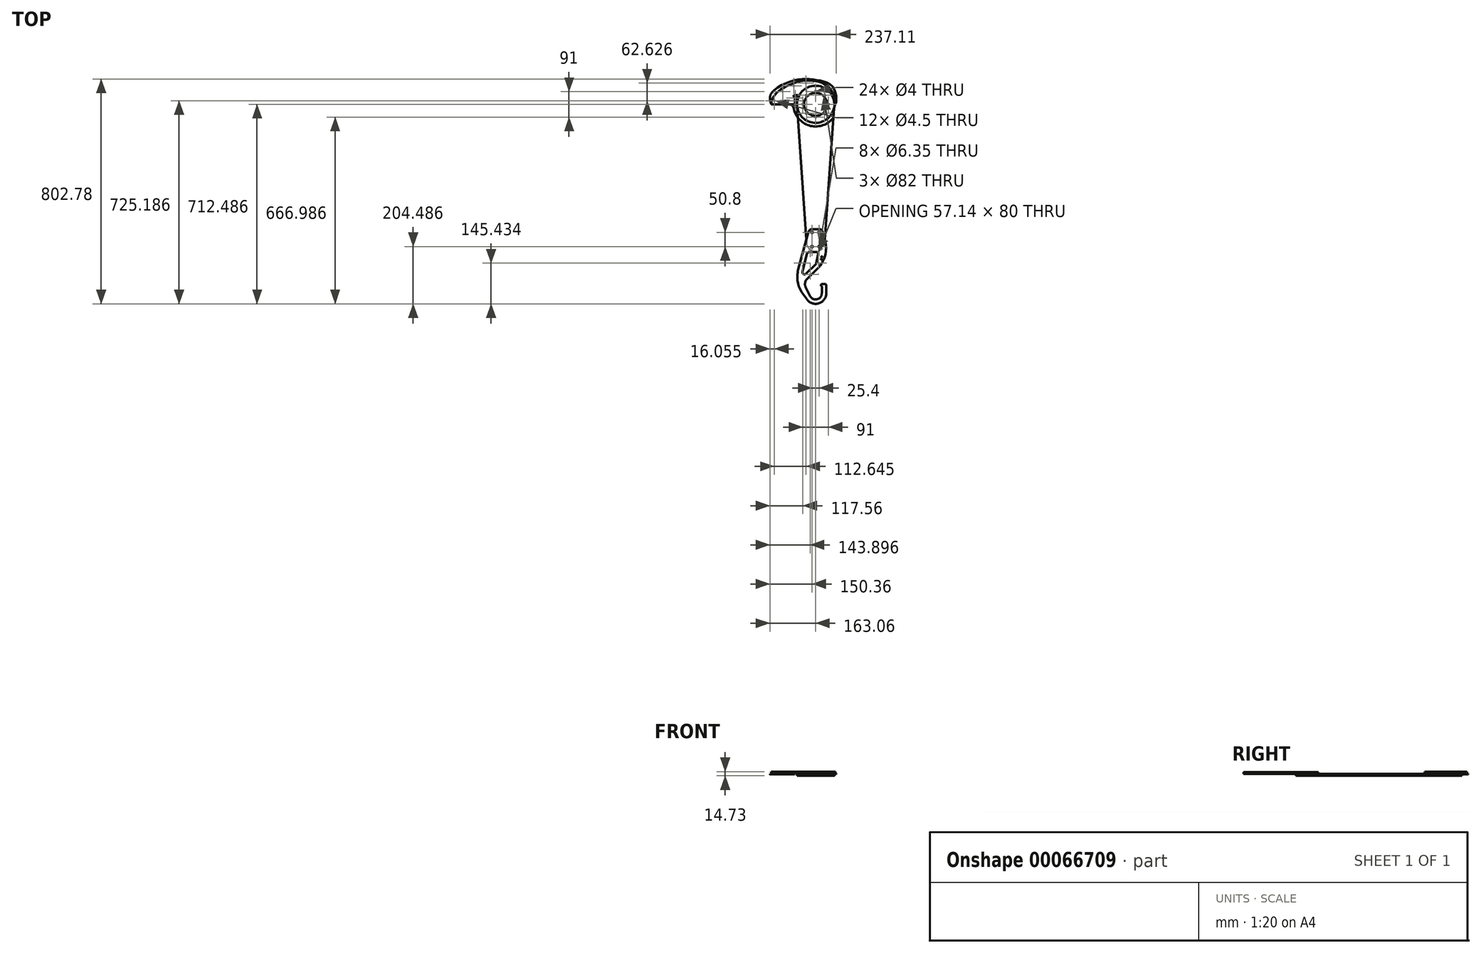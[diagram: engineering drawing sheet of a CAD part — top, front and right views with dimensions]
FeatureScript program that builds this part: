
annotation { "Feature Type Name" : "Feature", "Feature Type Description" : "" }
export const myFeature = defineFeature(function(context is Context, id is Id, definition is map)
    precondition{}
    {
        {
            var Q0;
            Q0=qCreatedBy(makeId("Top.planeOp"),FACE);
            var sketch = newSketch(context, id + "F0", { "sketchPlane" : qUnion([Q0])});
            skLineSegment(sketch, "E0", {"start": v(-316.24, 303.68) * mm, "end": v(-281.67, -188.68) * mm});
            skLineSegment(sketch, "E1", {"start": v(-218.33, -188.68) * mm, "end": v(-183.76, 303.68) * mm});
            skArc(sketch, "E2", {"start": v(-183.76, 303.68) * mm, "mid": v(-250, 374.73) * mm, "end": v(-316.24, 303.68) * mm});
            skArc(sketch, "E3", {"start": v(-281.67, -188.68) * mm, "mid": v(-250, -218.2) * mm, "end": v(-218.33, -188.68) * mm});
            skLineSegment(sketch, "E4.bottom", {"start": v(-237.3, -148.87) * mm, "end": v(-262.7, -148.87) * mm, "construction": true});
            skLineSegment(sketch, "E4.top", {"start": v(-237.3, -199.67) * mm, "end": v(-262.7, -199.67) * mm, "construction": true});
            skLineSegment(sketch, "E4.left", {"start": v(-237.3, -148.87) * mm, "end": v(-237.3, -199.67) * mm, "construction": true});
            skLineSegment(sketch, "E4.right", {"start": v(-262.7, -148.87) * mm, "end": v(-262.7, -199.67) * mm, "construction": true});
            skCircle(sketch, "E5", {"center": v(-237.3, -199.67) * mm, "radius": 3.18 * mm});
            skCircle(sketch, "E6", {"center": v(-237.3, -148.87) * mm, "radius": 3.18 * mm});
            skCircle(sketch, "E7", {"center": v(-262.7, -199.67) * mm, "radius": 3.18 * mm});
            skCircle(sketch, "E8", {"center": v(-262.7, -148.87) * mm, "radius": 3.18 * mm});
            skLineSegment(sketch, "E9", {"start": v(-250, -186.97) * mm, "end": v(-250, -317.53) * mm, "construction": true});
            skLineSegment(sketch, "E10", {"start": v(-204.75, -174.27) * mm, "end": v(-310.47, -174.27) * mm, "construction": true});
            skSolve(sketch);
        }
        {
            var Q0;
            Q0 = qSketchRegion(id + "F0", true);
            extrude(context, id + "F1", {"entities" : qUnion([Q0]), "depth" : 7.37 * mm});
        }
        {
            var Q0;
            Q0=makeQuery(id+"F1.opExtrude","CAP_FACE",FACE,{"disambiguationData":[OSD([sQuery(id+"F0.wireOp",EDGE,"E0"),sQuery(id+"F0.wireOp",EDGE,"E1"),sQuery(id+"F0.wireOp",EDGE,"E2"),sQuery(id+"F0.wireOp",EDGE,"E3")])],"isStart":false});
            var sketch = newSketch(context, id + "F2", { "sketchPlane" : qUnion([Q0])});
            skCircle(sketch, "E11", {"center": v(-250, 308.33) * mm, "radius": 41 * mm});
            skSolve(sketch);
        }
        {
            var Q0;
            Q0=makeQuery(id+"F2.imprint","IMPRINT",FACE,{"disambiguationData":[TD([[makeQuery(id+"F2.imprint","IMPRINT",EDGE,{"derivedFrom":sQuery(id+"F2.wireOp",EDGE,"E11")}),1.0]])]});
            extrude(context, id + "F3", {"entities" : qUnion([Q0]), "operationType" : NewBodyOperationType.REMOVE, "oppositeDirection" : true, "depth" : 25.4 * mm});
        }
        {
            var Q0;
            Q0=makeQuery(id+"F1.opExtrude","CAP_FACE",FACE,{"disambiguationData":[OSD([sQuery(id+"F0.wireOp",EDGE,"E0"),sQuery(id+"F0.wireOp",EDGE,"E1"),sQuery(id+"F0.wireOp",EDGE,"E2"),sQuery(id+"F0.wireOp",EDGE,"E3"),sQuery(id+"F0.wireOp",EDGE,"E5"),sQuery(id+"F0.wireOp",EDGE,"E6"),sQuery(id+"F0.wireOp",EDGE,"E7"),sQuery(id+"F0.wireOp",EDGE,"E8")])],"isStart":false});
            var sketch = newSketch(context, id + "F4", { "sketchPlane" : qUnion([Q0])});
            skLineSegment(sketch, "E12", {"start": v(-250, -72.28) * mm, "end": v(-250, -435.83) * mm, "construction": true});
            skCircle(sketch, "E13", {"center": v(-250, -366.06) * mm, "radius": 19.05 * mm, "construction": true});
            skCircle(sketch, "E14.0", {"center": v(-262.7, -148.87) * mm, "radius": 3.18 * mm});
            skCircle(sketch, "E14.1", {"center": v(-237.3, -148.87) * mm, "radius": 3.18 * mm});
            skCircle(sketch, "E14.2", {"center": v(-237.3, -199.67) * mm, "radius": 3.18 * mm});
            skCircle(sketch, "E14.3", {"center": v(-262.7, -199.67) * mm, "radius": 3.18 * mm});
            skCircle(sketch, "E15", {"center": v(-250, -366.06) * mm, "radius": 22.23 * mm});
            skLineSegment(sketch, "E16", {"start": v(-200.62, -235.34) * mm, "end": v(-293.23, -327.96) * mm});
            skLineSegment(sketch, "E17", {"start": v(-211.9, -241.78) * mm, "end": v(-211.9, -137.46) * mm, "construction": true});
            skLineSegment(sketch, "E18", {"start": v(-227.24, -137.46) * mm, "end": v(-272.76, -137.46) * mm});
            skLineSegment(sketch, "E19", {"start": v(-324.58, -327.96) * mm, "end": v(-280.87, -388.39) * mm});
            skArc(sketch, "E20", {"start": v(-280.87, -388.39) * mm, "mid": v(-238.26, -402.3) * mm, "end": v(-211.9, -366.06) * mm});
            skLineSegment(sketch, "E21", {"start": v(-211.9, -366.06) * mm, "end": v(-211.9, -333.02) * mm});
            skLineSegment(sketch, "E22", {"start": v(-211.9, -333.02) * mm, "end": v(-230.95, -333.02) * mm});
            skLineSegment(sketch, "E23", {"start": v(-230.95, -333.02) * mm, "end": v(-230.95, -339.37) * mm});
            skLineSegment(sketch, "E24", {"start": v(-230.95, -339.37) * mm, "end": v(-227.78, -339.37) * mm});
            skLineSegment(sketch, "E25", {"start": v(-227.78, -366.06) * mm, "end": v(-227.78, -339.37) * mm});
            skCircle(sketch, "E26", {"center": v(-229.53, -244.44) * mm, "radius": 1.75 * mm});
            skCircle(sketch, "E27", {"center": v(-227.78, -236.5) * mm, "radius": 1.75 * mm});
            skArc(sketch, "E28", {"start": v(-227.78, -345.72) * mm, "mid": v(-277.64, -333.68) * mm, "end": v(-316.5, -300.2) * mm, "construction": true});
            skCircle(sketch, "E29", {"center": v(-247.79, -316.19) * mm, "radius": 23.81 * mm, "construction": true});
            skLineSegment(sketch, "E30", {"start": v(-230.95, -333.02) * mm, "end": v(-264.63, -299.35) * mm, "construction": true});
            skLineSegment(sketch, "E31", {"start": v(-293.23, -327.96) * mm, "end": v(-269.99, -375.77) * mm});
            skPoint(sketch, "E32", {"position": v(-250, 308.33) * mm});
            skLineSegment(sketch, "E33", {"start": v(-272.76, -137.46) * mm, "end": v(-324.58, -327.96) * mm});
            skLineSegment(sketch, "E34", {"start": v(-227.24, -137.46) * mm, "end": v(-200.62, -235.34) * mm});
            skLineSegment(sketch, "E35", {"start": v(-284.2, -296.47) * mm, "end": v(-249.4, -261.67) * mm});
            skLineSegment(sketch, "E36", {"start": v(-272.35, -218.72) * mm, "end": v(-248.53, -218.72) * mm});
            skLineSegment(sketch, "E37.trimOffspring", {"start": v(-280, -224.58) * mm, "end": v(-297.47, -288.77) * mm});
            skLineSegment(sketch, "E38", {"start": v(-247.26, -257.77) * mm, "end": v(-240.78, -228.37) * mm});
            skPoint(sketch, "E39.visualSharp", {"position": v(-305.3, -317.58) * mm});
            skArc(sketch, "E39.filletArc", {"start": v(-297.47, -288.77) * mm, "mid": v(-293.8, -297.72) * mm, "end": v(-284.2, -296.47) * mm});
            skPoint(sketch, "E40.visualSharp", {"position": v(-278.41, -218.72) * mm});
            skArc(sketch, "E40.filletArc", {"start": v(-272.35, -218.72) * mm, "mid": v(-277.17, -220.36) * mm, "end": v(-280, -224.58) * mm});
            skPoint(sketch, "E41.visualSharp", {"position": v(-238.65, -218.72) * mm});
            skArc(sketch, "E41.filletArc", {"start": v(-240.78, -228.37) * mm, "mid": v(-242.34, -221.69) * mm, "end": v(-248.53, -218.72) * mm});
            skPoint(sketch, "E42.visualSharp", {"position": v(-247.76, -260.03) * mm});
            skArc(sketch, "E42.filletArc", {"start": v(-249.4, -261.67) * mm, "mid": v(-248.05, -259.87) * mm, "end": v(-247.26, -257.77) * mm});
            skSolve(sketch);
        }
        {
            var Q0;
            {var subQ8=sQuery(id+"F4.wireOp",EDGE,"E20");Q0=makeQuery(id+"F4.imprint","IMPRINT",FACE,{"disambiguationData":[TD([[makeQuery(id+"F4.imprint","IMPRINT",EDGE,{"derivedFrom":subQ8}),1.0]])]});}
            var Q1;
            Q1=makeQuery(id+"F4.imprint","IMPRINT",FACE,{"disambiguationData":[TD([[makeQuery(id+"F4.imprint","IMPRINT",EDGE,{"derivedFrom":sQuery(id+"F4.wireOp",EDGE,"E14.0")}),-1.0]])]});
            extrude(context, id + "F5", {"entities" : qUnion([Q0, Q1]), "depth" : 6.35 * mm});
        }
        {
            var Q0;
            Q0=makeQuery(id+"F5.opExtrude","SWEPT_EDGE",EDGE,{"disambiguationData":[OSD([sQuery(id+"F4.wireOp",EDGE,"E18"),sQuery(id+"F4.wireOp",EDGE,"E33")])]});
            var Q1;
            Q1=makeQuery(id+"F5.opExtrude","SWEPT_EDGE",EDGE,{"disambiguationData":[OSD([sQuery(id+"F4.wireOp",EDGE,"E18"),sQuery(id+"F4.wireOp",EDGE,"E34")])]});
            fillet(context, id + "F6", {"entities" : qUnion([Q0, Q1]), "radius" : 12.7 * mm, "tangentPropagation" : true, "allowEdgeOverflow" : false});
        }
        {
            var Q0;
            Q0=makeQuery(id+"F5.opExtrude","SWEPT_EDGE",EDGE,{"disambiguationData":[OSD([sQuery(id+"F4.wireOp",EDGE,"E16"),sQuery(id+"F4.wireOp",EDGE,"E31")])]});
            fillet(context, id + "F7", {"entities" : qUnion([Q0]), "radius" : 25.4 * mm, "tangentPropagation" : true, "allowEdgeOverflow" : false});
        }
        {
            var Q0;
            Q0=makeQuery(id+"F5.opExtrude","SWEPT_EDGE",EDGE,{"disambiguationData":[OSD([sQuery(id+"F4.wireOp",EDGE,"E16"),sQuery(id+"F4.wireOp",EDGE,"E17")])]});
            var Q1;
            Q1=makeQuery(id+"F5.opExtrude","SWEPT_EDGE",EDGE,{"disambiguationData":[OSD([sQuery(id+"F4.wireOp",EDGE,"E19"),sQuery(id+"F4.wireOp",EDGE,"E33")])]});
            fillet(context, id + "F8", {"entities" : qUnion([Q0, Q1]), "radius" : 101.6 * mm, "tangentPropagation" : true, "allowEdgeOverflow" : false});
        }
        {
            var Q0;
            Q0=makeQuery(id+"F5.opExtrude","SWEPT_EDGE",EDGE,{"disambiguationData":[OSD([sQuery(id+"F4.wireOp",EDGE,"E22"),sQuery(id+"F4.wireOp",EDGE,"E23")])]});
            var Q1;
            Q1=makeQuery(id+"F5.opExtrude","SWEPT_EDGE",EDGE,{"disambiguationData":[OSD([sQuery(id+"F4.wireOp",EDGE,"E21"),sQuery(id+"F4.wireOp",EDGE,"E22")])]});
            fillet(context, id + "F9", {"entities" : qUnion([Q0, Q1]), "radius" : 4.76 * mm, "tangentPropagation" : true, "allowEdgeOverflow" : false});
        }
        {
            var Q0;
            Q0=makeQuery(id+"F5.opExtrude","SWEPT_EDGE",EDGE,{"disambiguationData":[OSD([sQuery(id+"F4.wireOp",EDGE,"E24"),sQuery(id+"F4.wireOp",EDGE,"E25")])]});
            fillet(context, id + "F10", {"entities" : qUnion([Q0]), "radius" : 3.97 * mm, "tangentPropagation" : true, "allowEdgeOverflow" : false});
        }
        {
            var Q0;
            {var subQ0=makeQuery(id+"F1.opExtrude","CAP_EDGE",EDGE,{"disambiguationData":[OSD([sQuery(id+"F0.wireOp",EDGE,"E2")])],"isStart":false});Q0=makeQuery(id+"F4.imprint","IMPRINT",FACE,{"disambiguationData":[TD([[makeQuery(id+"F4.imprint","IMPRINT",EDGE,{"derivedFrom":subQ0}),1.0]])]});}
            var sketch = newSketch(context, id + "F11", { "sketchPlane" : qUnion([Q0])});
            skCircle(sketch, "E43.cCircle", {"center": v(-250, 308.33) * mm, "radius": 45.5 * mm, "construction": true});
            skLineSegment(sketch, "E43.0", {"start": v(-217.83, 276.15) * mm, "end": v(-250, 262.83) * mm, "construction": true});
            skLineSegment(sketch, "E43.1", {"start": v(-250, 262.83) * mm, "end": v(-282.17, 276.15) * mm, "construction": true});
            skLineSegment(sketch, "E43.2", {"start": v(-282.17, 276.15) * mm, "end": v(-295.5, 308.33) * mm, "construction": true});
            skLineSegment(sketch, "E43.3", {"start": v(-295.5, 308.33) * mm, "end": v(-282.17, 340.5) * mm, "construction": true});
            skLineSegment(sketch, "E43.4", {"start": v(-282.17, 340.5) * mm, "end": v(-250, 353.83) * mm, "construction": true});
            skLineSegment(sketch, "E43.5", {"start": v(-250, 353.83) * mm, "end": v(-217.83, 340.5) * mm, "construction": true});
            skLineSegment(sketch, "E43.6", {"start": v(-217.83, 340.5) * mm, "end": v(-204.5, 308.33) * mm, "construction": true});
            skLineSegment(sketch, "E43.7", {"start": v(-204.5, 308.33) * mm, "end": v(-217.83, 276.15) * mm, "construction": true});
            skCircle(sketch, "E44", {"center": v(-217.83, 276.15) * mm, "radius": 2 * mm});
            skCircle(sketch, "E45", {"center": v(-250, 262.83) * mm, "radius": 2 * mm});
            skCircle(sketch, "E46", {"center": v(-282.17, 276.15) * mm, "radius": 2 * mm});
            skCircle(sketch, "E47", {"center": v(-295.5, 308.33) * mm, "radius": 2 * mm});
            skCircle(sketch, "E48", {"center": v(-282.17, 340.5) * mm, "radius": 2 * mm});
            skCircle(sketch, "E49", {"center": v(-250, 353.83) * mm, "radius": 2 * mm});
            skCircle(sketch, "E50", {"center": v(-217.83, 340.5) * mm, "radius": 2 * mm});
            skCircle(sketch, "E51", {"center": v(-204.5, 308.33) * mm, "radius": 2 * mm});
            skSolve(sketch);
        }
        {
            var Q0;
            Q0 = qSketchRegion(id + "F11", true);
            extrude(context, id + "F12", {"entities" : qUnion([Q0]), "operationType" : NewBodyOperationType.REMOVE, "endBound" : BoundingType.THROUGH_ALL, "oppositeDirection" : true, "depth" : 25.4 * mm});
        }
        {
            var Q0;
            Q0=makeQuery(id+"F2.imprint","IMPRINT",FACE,{"disambiguationData":[TD([[makeQuery(id+"F2.imprint","IMPRINT",EDGE,{"derivedFrom":sQuery(id+"F2.wireOp",EDGE,"E11")}),-1.0]])]});
            var sketch = newSketch(context, id + "F13", { "sketchPlane" : qUnion([Q0])});
            skFitSpline(sketch, "E52", {"points": [v(-180.15, 308.33) * mm, v(-196.12, 362.2) * mm, v(-250, 390.88) * mm, v(-326.33, 384.66) * mm, v(-408.75, 308.33) * mm], "startDerivative": vector(54.67, 167.45) * mm, "endDerivative": vector(0, -373.77) * mm});
            skLineSegment(sketch, "E53", {"start": v(-408.75, 308.33) * mm, "end": v(-250, 308.33) * mm});
            skLineSegment(sketch, "E54", {"start": v(-250, 308.33) * mm, "end": v(-326.33, 384.66) * mm, "construction": true});
            skLineSegment(sketch, "E55", {"start": v(-250, 308.33) * mm, "end": v(-250, 390.88) * mm, "construction": true});
            skLineSegment(sketch, "E56", {"start": v(-250, 308.33) * mm, "end": v(-196.12, 362.2) * mm, "construction": true});
            skLineSegment(sketch, "E57", {"start": v(-250, 308.33) * mm, "end": v(-180.15, 308.33) * mm});
            skCircle(sketch, "E58", {"center": v(-250, 308.33) * mm, "radius": 66.4 * mm});
            skLineSegment(sketch, "E59", {"start": v(-186.88, 287.72) * mm, "end": v(-180.15, 308.33) * mm});
            skLineSegment(sketch, "E60", {"start": v(-324.34, 308.33) * mm, "end": v(-324.34, 333.73) * mm});
            skLineSegment(sketch, "E61", {"start": v(-316.4, 308.33) * mm, "end": v(-316.4, 333.73) * mm});
            skArc(sketch, "E62", {"start": v(-324.34, 341.66) * mm, "mid": v(-328.3, 337.7) * mm, "end": v(-324.34, 333.73) * mm});
            skArc(sketch, "E63", {"start": v(-316.4, 333.73) * mm, "mid": v(-312.43, 337.7) * mm, "end": v(-316.4, 341.66) * mm});
            skLineSegment(sketch, "E64", {"start": v(-324.34, 341.66) * mm, "end": v(-316.4, 341.66) * mm});
            skSolve(sketch);
        }
        {
            var Q0;
            {var subQ0=sQuery(id+"F13.wireOp",EDGE,"E52");Q0=makeQuery(id+"F13.imprint","IMPRINT",FACE,{"disambiguationData":[TD([[makeQuery(id+"F13.imprint","IMPRINT",EDGE,{"derivedFrom":subQ0}),1.0]])]});}
            var Q1;
            {var subQ3=sQuery(id+"F13.wireOp",EDGE,"E58");var subQ5=makeQuery(id+"F2.imprint","IMPRINT",EDGE,{"derivedFrom":makeQuery(id+"F1.opExtrude","CAP_EDGE",EDGE,{"disambiguationData":[OSD([sQuery(id+"F0.wireOp",EDGE,"E1")])],"isStart":false})});var subQ6=makeQuery(id+"F13.imprint","INTERSECT",VERTEX,{"derivedFrom":[subQ5,subQ3]});Q1=makeQuery(id+"F13.imprint","IMPRINT",FACE,{"disambiguationData":[TD([[makeQuery(id+"F13.imprint","IMPRINT",EDGE,{"disambiguationData":[TD([[subQ6,-1.0]])],"derivedFrom":subQ3}),-1.0]])]});}
            var Q2;
            {var subQ0=sQuery(id+"F13.wireOp",EDGE,"E58");var subQ1=makeQuery(id+"F2.imprint","IMPRINT",EDGE,{"derivedFrom":makeQuery(id+"F1.opExtrude","CAP_EDGE",EDGE,{"disambiguationData":[OSD([sQuery(id+"F0.wireOp",EDGE,"E1")])],"isStart":false})});var subQ2=makeQuery(id+"F13.imprint","INTERSECT",VERTEX,{"derivedFrom":[subQ1,subQ0]});Q2=makeQuery(id+"F13.imprint","IMPRINT",FACE,{"disambiguationData":[TD([[makeQuery(id+"F13.imprint","IMPRINT",EDGE,{"disambiguationData":[TD([[subQ2,1.0]])],"derivedFrom":subQ0}),-1.0]])]});}
            var Q3;
            {var subQ0=sQuery(id+"F13.wireOp",EDGE,"E58");var subQ6=sQuery(id+"F13.wireOp",EDGE,"E53");var subQ7=makeQuery(id+"F13.imprint","INTERSECT",VERTEX,{"derivedFrom":[subQ6,subQ0]});Q3=makeQuery(id+"F13.imprint","IMPRINT",FACE,{"disambiguationData":[TD([[makeQuery(id+"F13.imprint","IMPRINT",EDGE,{"disambiguationData":[TD([[subQ7,-1.0]])],"derivedFrom":subQ6}),-1.0]])]});}
            var Q4;
            {var subQ0=sQuery(id+"F13.wireOp",EDGE,"E58");var subQ1=sQuery(id+"F13.wireOp",EDGE,"E53");var subQ2=makeQuery(id+"F13.imprint","INTERSECT",VERTEX,{"derivedFrom":[subQ1,subQ0]});Q4=makeQuery(id+"F13.imprint","IMPRINT",FACE,{"disambiguationData":[TD([[makeQuery(id+"F13.imprint","IMPRINT",EDGE,{"disambiguationData":[TD([[subQ2,-1.0]])],"derivedFrom":subQ1}),1.0]])]});}
            extrude(context, id + "F14", {"entities" : qUnion([Q0, Q1, Q2, Q3, Q4]), "depth" : 7.37 * mm});
        }
        {
            var Q0;
            Q0 = qSketchRegion(id + "F11", true);
            extrude(context, id + "F15", {"entities" : qUnion([Q0]), "operationType" : NewBodyOperationType.REMOVE, "endBound" : BoundingType.THROUGH_ALL, "depth" : 25.4 * mm});
        }
        {
            var Q0;
            Q0=makeQuery(id+"F14.opExtrude","CAP_FACE",FACE,{"disambiguationData":[OSD([sQuery(id+"F2.wireOp",EDGE,"E11"),sQuery(id+"F13.wireOp",EDGE,"E52"),sQuery(id+"F13.wireOp",EDGE,"E53"),sQuery(id+"F13.wireOp",EDGE,"E58"),sQuery(id+"F13.wireOp",EDGE,"E59"),sQuery(id+"F13.wireOp",EDGE,"E60"),sQuery(id+"F13.wireOp",EDGE,"E61"),sQuery(id+"F13.wireOp",EDGE,"E62"),sQuery(id+"F13.wireOp",EDGE,"E63"),sQuery(id+"F13.wireOp",EDGE,"E64")])],"isStart":true});
            var sketch = newSketch(context, id + "F16", { "sketchPlane" : qUnion([Q0])});
            skLineSegment(sketch, "E65.0.0", {"start": v(-180.15, -308.33) * mm, "end": v(-186.88, -287.72) * mm});
            skArc(sketch, "E65.0.1", {"start": v(-186.88, -287.72) * mm, "mid": v(-260.43, -242.75) * mm, "end": v(-316.4, -308.33) * mm});
            skLineSegment(sketch, "E65.0.2", {"start": v(-316.4, -308.33) * mm, "end": v(-316.4, -333.73) * mm});
            skArc(sketch, "E65.0.3", {"start": v(-316.4, -333.73) * mm, "mid": v(-312.43, -337.7) * mm, "end": v(-316.4, -341.66) * mm});
            skLineSegment(sketch, "E65.0.4", {"start": v(-316.4, -341.66) * mm, "end": v(-324.34, -341.66) * mm});
            skArc(sketch, "E65.0.5", {"start": v(-324.34, -341.66) * mm, "mid": v(-328.3, -337.7) * mm, "end": v(-324.34, -333.73) * mm});
            skLineSegment(sketch, "E65.0.6", {"start": v(-324.34, -333.73) * mm, "end": v(-324.34, -308.33) * mm});
            skLineSegment(sketch, "E65.0.7", {"start": v(-316.4, -308.33) * mm, "end": v(-421.45, -308.33) * mm});
            skFitSpline(sketch, "E65.0.8", {"points": [v(-408.75, -308.33) * mm, v(-408.75, -346.43) * mm, v(-324.68, -394.08) * mm, v(-251.96, -395.6) * mm, v(-190.44, -372.08) * mm, v(-176.2, -320.4) * mm, v(-180.15, -308.33) * mm]});
            skArc(sketch, "E66.0", {"start": v(-183.76, -303.68) * mm, "mid": v(-250, -374.73) * mm, "end": v(-316.24, -303.68) * mm});
            skLineSegment(sketch, "E67.0", {"start": v(-218.33, 188.68) * mm, "end": v(-183.76, -303.68) * mm});
            skFitSpline(sketch, "E68.0", {"points": [v(-421.45, -308.33) * mm, v(-421.45, -310.8) * mm, v(-421.14, -315.67) * mm, v(-419.82, -322.74) * mm, v(-417.72, -329.49) * mm, v(-414, -338.02) * mm, v(-407.82, -347.8) * mm, v(-398.62, -358.14) * mm, v(-388.08, -367.27) * mm, v(-376.6, -375.3) * mm, v(-364.48, -382.31) * mm, v(-354.15, -387.36) * mm, v(-345.9, -390.92) * mm, v(-339.77, -393.37) * mm, v(-333.72, -395.58) * mm, v(-327.81, -397.57) * mm, v(-322.03, -399.33) * mm, v(-314.48, -401.4) * mm, v(-305.33, -403.45) * mm, v(-294.75, -405.12) * mm, v(-284.52, -406.03) * mm, v(-274.6, -406.23) * mm, v(-266.58, -405.86) * mm, v(-260.29, -405.27) * mm, v(-255.62, -404.68) * mm, v(-251.77, -404.1) * mm, v(-248.71, -403.56) * mm, v(-245.67, -402.99) * mm, v(-241.85, -402.2) * mm, v(-235.73, -400.72) * mm, v(-228.09, -398.5) * mm, v(-219.02, -395.05) * mm, v(-210.18, -390.7) * mm, v(-203.1, -386.2) * mm, v(-197.71, -382.02) * mm, v(-193.83, -378.58) * mm, v(-190.74, -375.45) * mm, v(-188.37, -372.8) * mm, v(-186.65, -370.73) * mm, v(-184.98, -368.57) * mm, v(-182.86, -365.64) * mm, v(-180.4, -361.84) * mm, v(-177.7, -357.13) * mm, v(-174.48, -350.7) * mm, v(-171.13, -342.47) * mm, v(-168.21, -332.57) * mm, v(-166.78, -324.51) * mm, v(-166.32, -318.22) * mm, v(-166.35, -313.58) * mm, v(-166.85, -308.98) * mm, v(-167.58, -305.92) * mm, v(-168.08, -304.38) * mm]});
            skFitSpline(sketch, "E69.0", {"points": [v(-399.22, -308.33) * mm, v(-399.22, -309.88) * mm, v(-399.03, -312.93) * mm, v(-398.2, -317.35) * mm, v(-396.86, -321.68) * mm, v(-394.39, -327.34) * mm, v(-390.06, -334.25) * mm, v(-383.04, -342.2) * mm, v(-374.46, -349.65) * mm, v(-364.68, -356.5) * mm, v(-354.05, -362.66) * mm, v(-342.96, -368.08) * mm, v(-333.66, -371.93) * mm, v(-326.36, -374.6) * mm, v(-321.02, -376.4) * mm, v(-315.84, -377.97) * mm, v(-309.14, -379.8) * mm, v(-297.92, -382.32) * mm, v(-286.1, -383.76) * mm, v(-274.9, -383.98) * mm, v(-268.09, -383.67) * mm, v(-262.7, -383.16) * mm, v(-258.7, -382.66) * mm, v(-255.35, -382.15) * mm, v(-252.68, -381.68) * mm, v(-250.01, -381.18) * mm, v(-246.7, -380.49) * mm, v(-241.48, -379.24) * mm, v(-235.12, -377.38) * mm, v(-227.86, -374.61) * mm, v(-221.05, -371.25) * mm, v(-215.81, -367.91) * mm, v(-211.9, -364.88) * mm, v(-209.11, -362.41) * mm, v(-206.9, -360.18) * mm, v(-205.22, -358.29) * mm, v(-204, -356.81) * mm, v(-202.8, -355.27) * mm, v(-201.25, -353.12) * mm, v(-199.4, -350.27) * mm, v(-197.32, -346.64) * mm, v(-194.8, -341.6) * mm, v(-192.13, -335.09) * mm, v(-189.88, -327.39) * mm, v(-188.85, -321.5) * mm, v(-188.56, -317.43) * mm, v(-188.6, -314.78) * mm, v(-188.84, -312.65) * mm, v(-189.09, -311.66) * mm, v(-189.21, -311.28) * mm], "construction": true});
            skCircle(sketch, "E70", {"center": v(-397, -321.03) * mm, "radius": 2.25 * mm});
            skCircle(sketch, "E71", {"center": v(-367.6, -354.37) * mm, "radius": 2.25 * mm});
            skCircle(sketch, "E72", {"center": v(-327.77, -374.07) * mm, "radius": 2.25 * mm});
            skCircle(sketch, "E73", {"center": v(-284.36, -383.65) * mm, "radius": 2.25 * mm});
            skCircle(sketch, "E74", {"center": v(-322.09, -330.55) * mm, "radius": 2.25 * mm});
            skCircle(sketch, "E75", {"center": v(-322.09, -321.03) * mm, "radius": 2.25 * mm});
            skArc(sketch, "E76.0", {"start": v(-186.77, -260.8) * mm, "mid": v(-275.06, -233.3) * mm, "end": v(-329.1, -308.33) * mm});
            skFitSpline(sketch, "E77", {"points": [v(-166.72, -322.96) * mm, v(-186.77, -260.8) * mm], "startDerivative": vector(7.2, 65.86) * mm, "endDerivative": vector(-39.81, 52.96) * mm});
            skLineSegment(sketch, "E78.0", {"start": v(-316.24, -303.68) * mm, "end": v(-281.67, 188.68) * mm});
            skSolve(sketch);
        }
        {
            var Q0;
            {var subQ0=sQuery(id+"F16.wireOp",EDGE,"E65.0.8");Q0=makeQuery(id+"F16.imprint","IMPRINT",FACE,{"disambiguationData":[TD([[makeQuery(id+"F16.imprint","IMPRINT",EDGE,{"derivedFrom":subQ0}),1.0]])]});}
            var Q1;
            {var subQ8=sQuery(id+"F16.wireOp",EDGE,"E65.0.2");Q1=makeQuery(id+"F16.imprint","IMPRINT",FACE,{"disambiguationData":[TD([[makeQuery(id+"F16.imprint","IMPRINT",EDGE,{"derivedFrom":subQ8}),1.0]])]});}
            var Q2;
            {var subQ1=sQuery(id+"F16.wireOp",EDGE,"E65.0.7");var subQ5=sQuery(id+"F16.wireOp",EDGE,"E76.0");var subQ6=makeQuery(id+"F16.imprint","INTERSECT",VERTEX,{"derivedFrom":[subQ1,subQ5]});Q2=makeQuery(id+"F16.imprint","IMPRINT",FACE,{"disambiguationData":[TD([[makeQuery(id+"F16.imprint","IMPRINT",EDGE,{"disambiguationData":[TD([[subQ6,-1.0]])],"derivedFrom":subQ1}),1.0]])]});}
            var Q3;
            {var subQ3=sQuery(id+"F16.wireOp",EDGE,"E65.0.2");Q3=makeQuery(id+"F16.imprint","IMPRINT",FACE,{"disambiguationData":[TD([[makeQuery(id+"F16.imprint","IMPRINT",EDGE,{"derivedFrom":subQ3}),-1.0]])]});}
            extrude(context, id + "F17", {"entities" : qUnion([Q0, Q1, Q2, Q3]), "depth" : 2.38 * mm});
        }
        {
            var Q0;
            {var subQ8=sQuery(id+"F16.wireOp",EDGE,"E65.0.2");Q0=makeQuery(id+"F16.imprint","IMPRINT",FACE,{"disambiguationData":[TD([[makeQuery(id+"F16.imprint","IMPRINT",EDGE,{"derivedFrom":subQ8}),1.0]])]});}
            var Q1;
            {var subQ6=sQuery(id+"F16.wireOp",EDGE,"E65.0.1");Q1=makeQuery(id+"F16.imprint","IMPRINT",FACE,{"disambiguationData":[TD([[makeQuery(id+"F16.imprint","IMPRINT",EDGE,{"derivedFrom":subQ6}),-1.0]])]});}
            var Q2;
            {var subQ0=sQuery(id+"F16.wireOp",EDGE,"E65.0.8");Q2=makeQuery(id+"F16.imprint","IMPRINT",FACE,{"disambiguationData":[TD([[makeQuery(id+"F16.imprint","IMPRINT",EDGE,{"derivedFrom":subQ0}),1.0]])]});}
            var Q3;
            {var subQ7=sQuery(id+"F16.wireOp",EDGE,"E65.0.1");Q3=makeQuery(id+"F16.imprint","IMPRINT",FACE,{"disambiguationData":[TD([[makeQuery(id+"F16.imprint","IMPRINT",EDGE,{"derivedFrom":subQ7}),1.0]])]});}
            var Q4;
            {var subQ3=sQuery(id+"F16.wireOp",EDGE,"E65.0.2");Q4=makeQuery(id+"F16.imprint","IMPRINT",FACE,{"disambiguationData":[TD([[makeQuery(id+"F16.imprint","IMPRINT",EDGE,{"derivedFrom":subQ3}),-1.0]])]});}
            var Q5;
            {var subQ1=sQuery(id+"F16.wireOp",EDGE,"E65.0.7");var subQ5=sQuery(id+"F16.wireOp",EDGE,"E76.0");var subQ6=makeQuery(id+"F16.imprint","INTERSECT",VERTEX,{"derivedFrom":[subQ1,subQ5]});Q5=makeQuery(id+"F16.imprint","IMPRINT",FACE,{"disambiguationData":[TD([[makeQuery(id+"F16.imprint","IMPRINT",EDGE,{"disambiguationData":[TD([[subQ6,-1.0]])],"derivedFrom":subQ1}),1.0]])]});}
            extrude(context, id + "F18", {"entities" : qUnion([Q0, Q1, Q2, Q3, Q4, Q5]), "depth" : 2.38 * mm});
        }
        {
            var Q0;
            Q0=makeQuery(id+"F17.opExtrude","SWEPT_EDGE",EDGE,{"disambiguationData":[OSD([sQuery(id+"F16.wireOp",EDGE,"E65.0.7"),sQuery(id+"F16.wireOp",EDGE,"E76.0")])]});
            var Q1;
            Q1=makeQuery(id+"F18.opExtrude","SWEPT_EDGE",EDGE,{"disambiguationData":[OSD([sQuery(id+"F16.wireOp",EDGE,"E65.0.7"),sQuery(id+"F16.wireOp",EDGE,"E76.0")])]});
            fillet(context, id + "F19", {"entities" : qUnion([Q0, Q1]), "radius" : 19.05 * mm, "tangentPropagation" : true, "allowEdgeOverflow" : false});
        }
        {
            var Q0;
            Q0=makeQuery(id+"F17.opExtrude","SWEPT_EDGE",EDGE,{"disambiguationData":[OSD([sQuery(id+"F16.wireOp",EDGE,"E76.0"),sQuery(id+"F16.wireOp",EDGE,"E78.0")])]});
            var Q1;
            Q1=makeQuery(id+"F17.opExtrude","SWEPT_EDGE",EDGE,{"disambiguationData":[OSD([sQuery(id+"F16.wireOp",EDGE,"E67.0"),sQuery(id+"F16.wireOp",EDGE,"E76.0"),sQuery(id+"F16.wireOp",EDGE,"E77")])]});
            var Q2;
            Q2=makeQuery(id+"F18.opExtrude","SWEPT_EDGE",EDGE,{"disambiguationData":[OSD([sQuery(id+"F16.wireOp",EDGE,"E65.0.7"),sQuery(id+"F16.wireOp",EDGE,"E68.0")])]});
            var Q3;
            Q3=makeQuery(id+"F17.opExtrude","SWEPT_EDGE",EDGE,{"disambiguationData":[OSD([sQuery(id+"F16.wireOp",EDGE,"E65.0.7"),sQuery(id+"F16.wireOp",EDGE,"E68.0")])]});
            fillet(context, id + "F20", {"entities" : qUnion([Q0, Q1, Q2, Q3]), "radius" : 5.08 * mm, "tangentPropagation" : true, "allowEdgeOverflow" : false});
        }
    });
